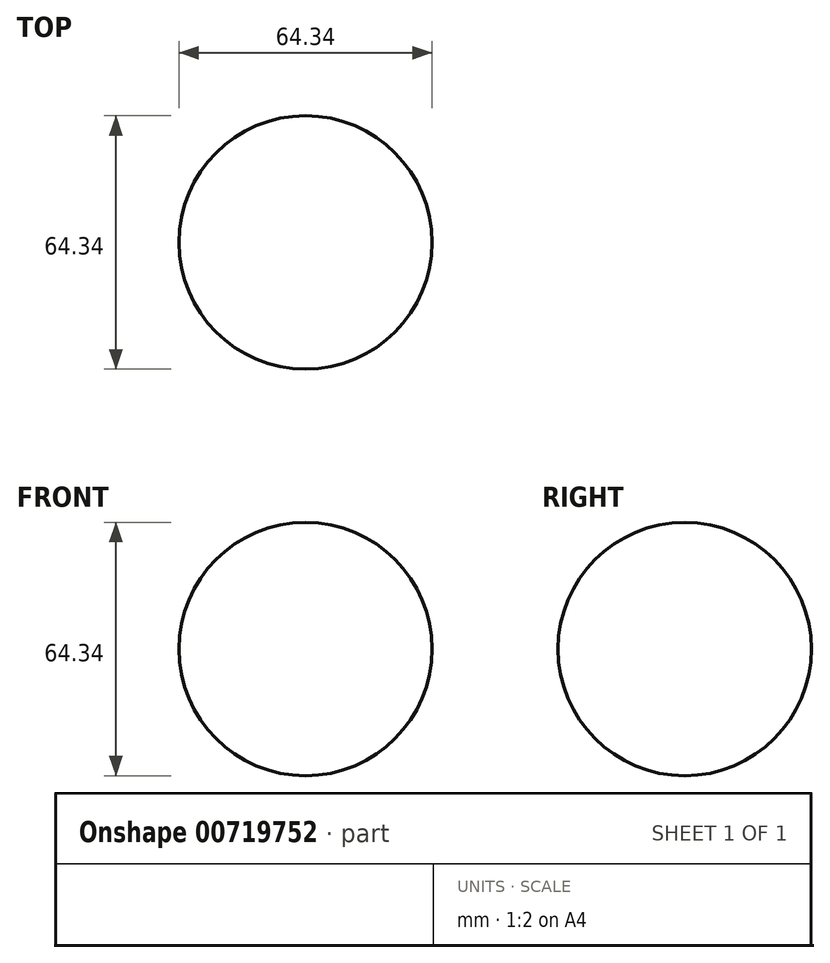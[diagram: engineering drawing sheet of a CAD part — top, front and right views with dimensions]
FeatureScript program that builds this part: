
annotation { "Feature Type Name" : "Feature", "Feature Type Description" : "" }
export const myFeature = defineFeature(function(context is Context, id is Id, definition is map)
    precondition{}
    {
        {
            var Q0;
            Q0=qCreatedBy(makeId("Front.planeOp"),FACE);
            var sketch = newSketch(context, id + "F0", { "sketchPlane" : qUnion([Q0])});
            skArc(sketch, "E0", {"start": v(32.17, 0) * mm, "mid": v(0, 32.17) * mm, "end": v(-32.17, 0) * mm});
            skLineSegment(sketch, "E1", {"start": v(-32.17, 0) * mm, "end": v(32.17, 0) * mm});
            skSolve(sketch);
        }
        {
            var Q0;
            Q0=sQuery(id+"F0.wireOp",EDGE,"E0");
            var Q1;
            Q1=sQuery(id+"F0.wireOp",EDGE,"E1");
            revolve(context, id + "F1", {"bodyType" : ToolBodyType.SURFACE, "surfaceOperationType" : NewSurfaceOperationType.NEW, "surfaceEntities" : qUnion([Q0]), "axis" : qUnion([Q1]), "revolveType" : RevolveType.FULL});
        }
    });
